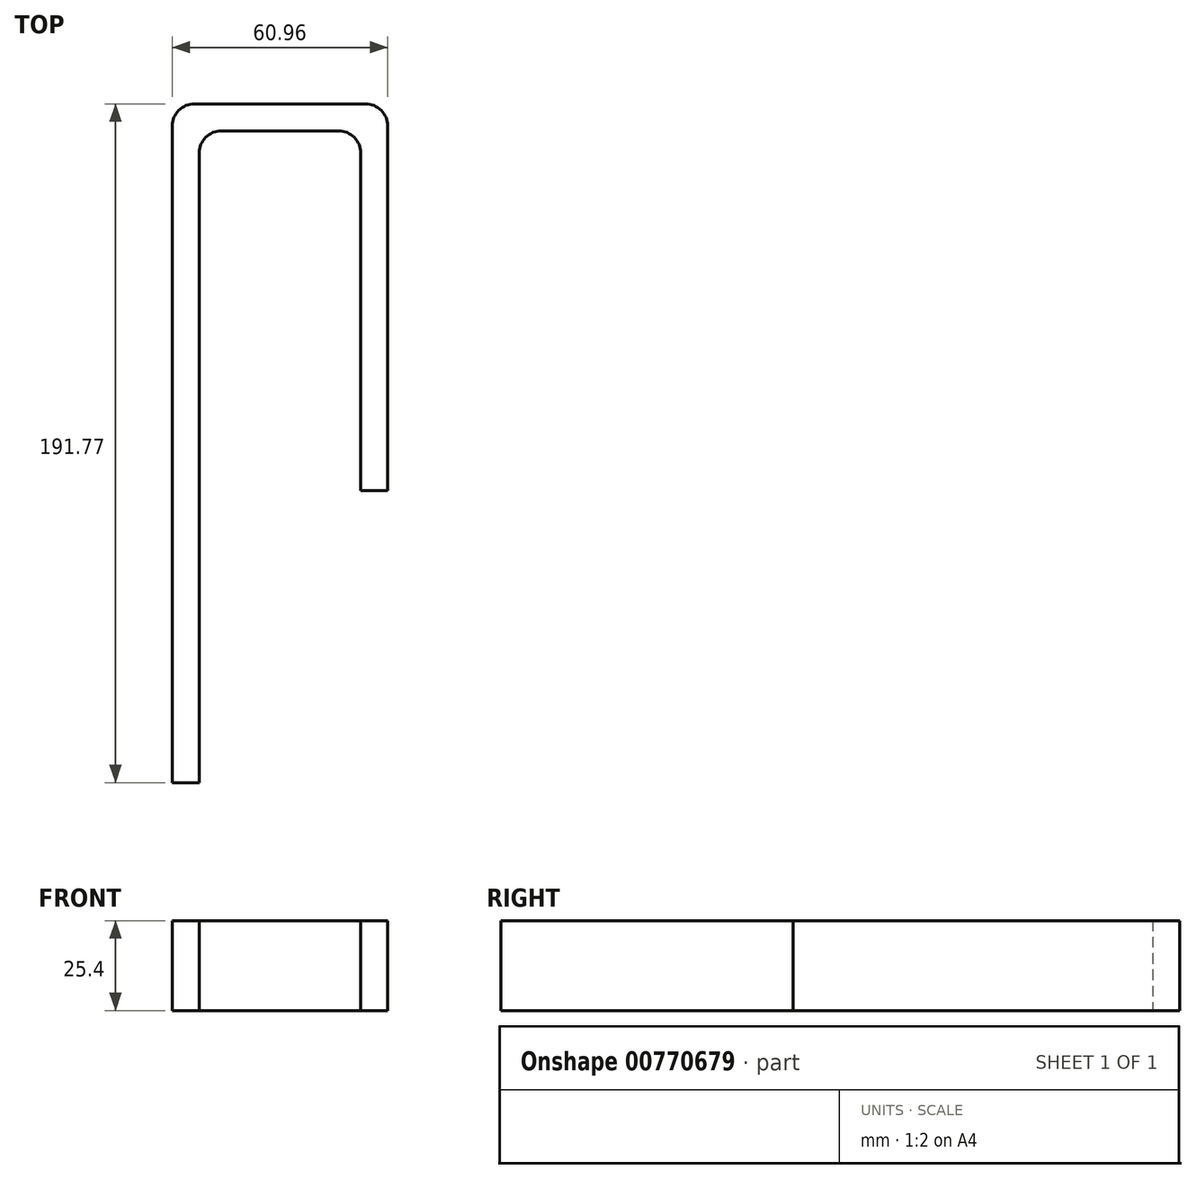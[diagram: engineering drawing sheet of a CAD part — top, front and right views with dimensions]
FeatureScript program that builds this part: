
annotation { "Feature Type Name" : "Feature", "Feature Type Description" : "" }
export const myFeature = defineFeature(function(context is Context, id is Id, definition is map)
    precondition{}
    {
        {
            var Q0;
            Q0=qCreatedBy(makeId("Top.planeOp"),FACE);
            var sketch = newSketch(context, id + "F0", { "sketchPlane" : qUnion([Q0])});
            skLineSegment(sketch, "E0", {"start": v(6.35, 0) * mm, "end": v(39.37, 0) * mm});
            skLineSegment(sketch, "E1", {"start": v(45.72, -6.35) * mm, "end": v(45.72, -101.6) * mm});
            skLineSegment(sketch, "E2", {"start": v(0, -6.35) * mm, "end": v(0, -184.15) * mm});
            skLineSegment(sketch, "E3.0", {"start": v(-7.62, 1.27) * mm, "end": v(-7.62, -184.15) * mm});
            skLineSegment(sketch, "E4.0", {"start": v(-1.27, 7.62) * mm, "end": v(47, 7.62) * mm});
            skLineSegment(sketch, "E5.0", {"start": v(53.34, 1.27) * mm, "end": v(53.34, -101.6) * mm});
            skLineSegment(sketch, "E6", {"start": v(-7.62, -184.15) * mm, "end": v(0, -184.15) * mm});
            skLineSegment(sketch, "E7", {"start": v(45.72, -101.6) * mm, "end": v(53.34, -101.6) * mm});
            skPoint(sketch, "E8.visualSharp", {"position": v(0, 0) * mm});
            skArc(sketch, "E8.filletArc", {"start": v(6.35, 0) * mm, "mid": v(1.86, -1.86) * mm, "end": v(0, -6.35) * mm});
            skPoint(sketch, "E9.visualSharp", {"position": v(45.72, 0) * mm});
            skArc(sketch, "E9.filletArc", {"start": v(45.72, -6.35) * mm, "mid": v(43.86, -1.86) * mm, "end": v(39.37, 0) * mm});
            skPoint(sketch, "E10.visualSharp", {"position": v(53.34, 7.62) * mm});
            skArc(sketch, "E10.filletArc", {"start": v(53.34, 1.27) * mm, "mid": v(51.48, 5.76) * mm, "end": v(47, 7.62) * mm});
            skPoint(sketch, "E11.visualSharp", {"position": v(-7.62, 7.62) * mm});
            skArc(sketch, "E11.filletArc", {"start": v(-1.27, 7.62) * mm, "mid": v(-5.76, 5.76) * mm, "end": v(-7.62, 1.27) * mm});
            skSolve(sketch);
        }
        {
            var Q0;
            Q0 = qSketchRegion(id + "F0", true);
            extrude(context, id + "F1", {"entities" : qUnion([Q0]), "depth" : 25.4 * mm, "offsetDistance" : 25.4 * mm});
        }
    });
